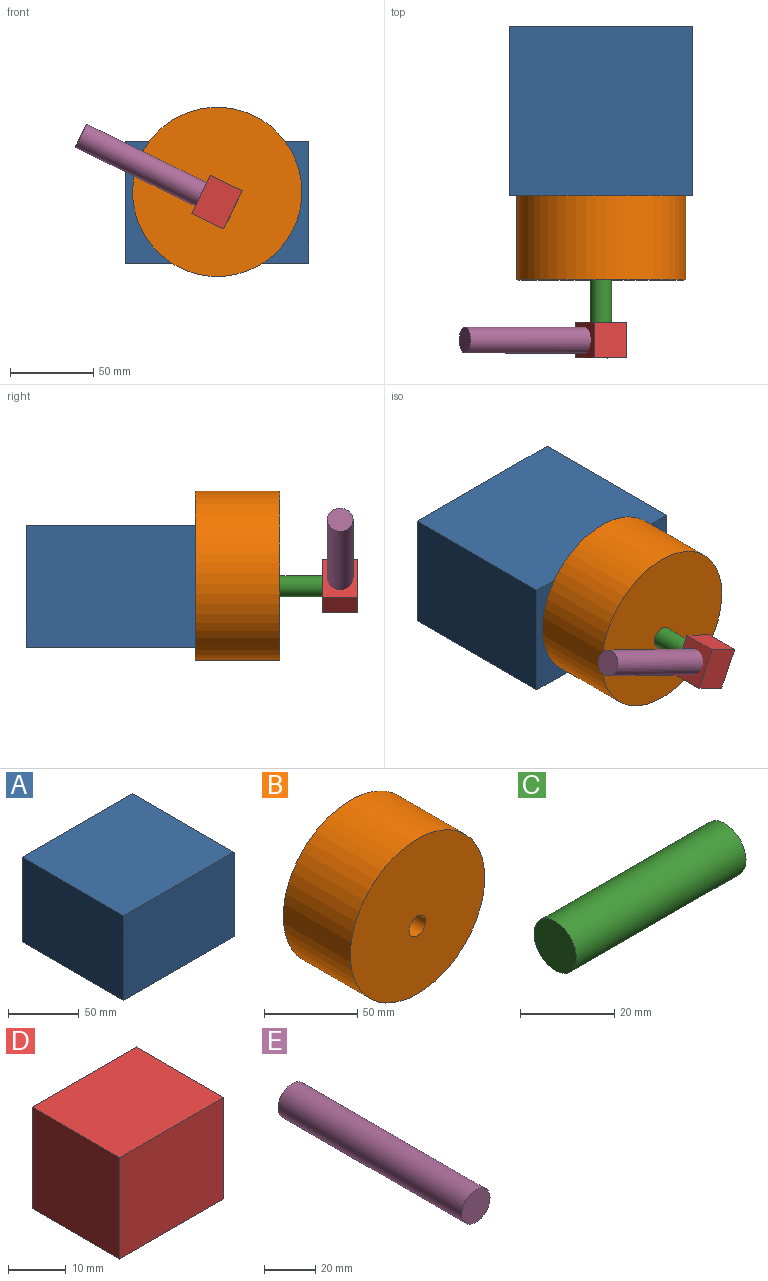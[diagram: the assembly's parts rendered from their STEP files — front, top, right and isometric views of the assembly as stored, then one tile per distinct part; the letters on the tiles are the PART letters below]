
ASSEMBLY  parts=5 mates=4
PART A: 6 faces, bbox 110.2x101.6x73.2 mm
  f0: plane 110.21x101.6mm, normal (0,0,1), area 11197.8mm2, adj f1,f3,f4,f5
  f1: plane 101.6x73.23mm, normal (-1,0,0), area 7440.1mm2, adj f0,f2,f4,f5
  f2: plane 110.21x101.6mm, normal (0,0,-1), area 11197.8mm2, adj f1,f3,f4,f5
  f3: plane 101.6x73.23mm, normal (1,0,0), area 7440.1mm2, adj f0,f2,f4,f5
  f4: plane 110.21x73.23mm, normal (0,-1,0), area 8070.9mm2, adj f0,f1,f2,f3
  f5: plane 110.21x73.23mm, normal (0,1,0), area 8070.9mm2, adj f0,f1,f2,f3
PART B: 4 faces, bbox 101.6x50.8x101.6 mm
  f0: cylinder r=50.8mm len=101.6mm, axis (0,1,0), area 16215.2mm2, adj f1,f2
  f1: plane 101.6x101.6mm, normal (0,-1,0), area 7981.2mm2, adj f0,f3
  f2: plane 101.6x101.6mm, normal (0,1,0), area 7981.2mm2, adj f0,f3
  f3: cylinder r=6.35mm len=50.8mm, axis (0,-1,0), area 2026.8mm2, adj f1,f2
PART C: 3 faces, bbox 50.8x12.7x12.7 mm
  f0: cylinder r=6.35mm len=50.8mm, axis (-1,0,0), area 2026.9mm2, adj f1,f2
  f1: plane 12.7x12.7mm, normal (1,0,0), area 126.7mm2, adj f0
  f2: plane 12.7x12.7mm, normal (-1,0,0), area 126.7mm2, adj f0
PART D: 6 faces, bbox 25.4x21.4x21.4 mm
  f0: plane 25.4x21.4mm, normal (0,0,1), area 543.5mm2, adj f1,f3,f4,f5
  f1: plane 25.4x21.4mm, normal (0,-1,0), area 543.5mm2, adj f0,f2,f4,f5
  f2: plane 25.4x21.4mm, normal (0,0,-1), area 543.5mm2, adj f1,f3,f4,f5
  f3: plane 25.4x21.4mm, normal (0,1,0), area 543.5mm2, adj f0,f2,f4,f5
  f4: plane 21.4x21.4mm, normal (1,0,0), area 457.9mm2, adj f0,f1,f2,f3
  f5: plane 21.4x21.4mm, normal (-1,0,0), area 457.9mm2, adj f0,f1,f2,f3
PART E: 3 faces, bbox 15.5x101.6x15.5 mm
  f0: cylinder r=7.77mm len=101.6mm, axis (0,1,0), area 4963mm2, adj f1,f2
  f1: plane 15.55x15.55mm, normal (0,-1,0), area 189.9mm2, adj f0
  f2: plane 15.55x15.55mm, normal (0,1,0), area 189.9mm2, adj f0
PLACE A t=(-129.01,96.28,22)mm
PLACE B t=(-58.42,-5.32,-8.1)mm fixed
PLACE C rot(axis=(0.22,0.22,0.95),92.9deg) t=(-148.97,-81.52,-7.78)mm
PLACE D rot(axis=(0,1,0),116deg) t=(-109.96,-68.85,10.85)mm
PLACE E rot(axis=(-0.4,0.65,0.65),136deg) t=(-169.77,-101.83,87.93)mm
MATE revolute C.f0 <-> B.f3  axis (0,-1,0) through (-112.49,-56.12,-2.04)mm
MATE fastened D.f3 <-> C.f0  axis (0,1,0) through (-112.49,-81.52,-2.04)mm
MATE fastened E.f0 <-> D.f0  axis (0.9,0,-0.44) through (-102.88,-92.22,-6.73)mm
MATE fastened B.f3 <-> A.f4  axis (0,1,0) through (-112.49,-5.32,-2.04)mm
